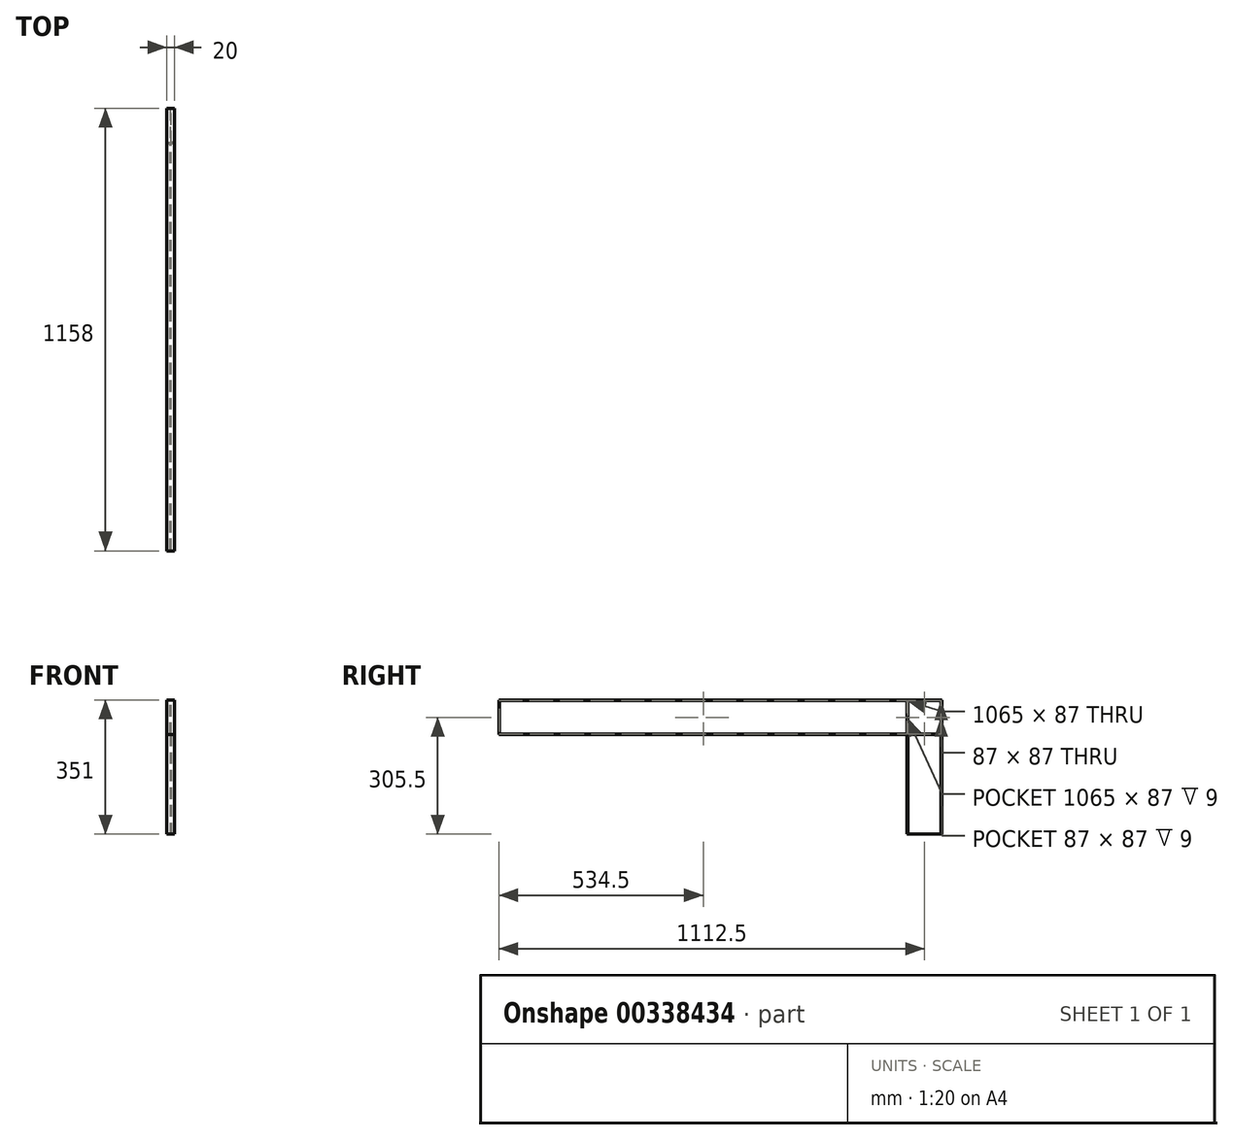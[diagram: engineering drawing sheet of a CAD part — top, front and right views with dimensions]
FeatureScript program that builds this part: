
annotation { "Feature Type Name" : "Feature", "Feature Type Description" : "" }
export const myFeature = defineFeature(function(context is Context, id is Id, definition is map)
    precondition{}
    {
        {
            var Q0;
            Q0=qCreatedBy(makeId("Top.planeOp"),FACE);
            var sketch = newSketch(context, id + "F0", { "sketchPlane" : qUnion([Q0])});
            skLineSegment(sketch, "E0.bottom", {"start": v(0, 0) * mm, "end": v(-20, 0) * mm});
            skLineSegment(sketch, "E0.top", {"start": v(0, 91) * mm, "end": v(-20, 91) * mm});
            skLineSegment(sketch, "E0.left", {"start": v(0, 0) * mm, "end": v(0, 2) * mm});
            skLineSegment(sketch, "E0.right", {"start": v(-20, 0) * mm, "end": v(-20, 2) * mm});
            skLineSegment(sketch, "E1", {"start": v(-20, 89) * mm, "end": v(-11, 89) * mm});
            skLineSegment(sketch, "E2", {"start": v(-20, 2) * mm, "end": v(-11, 2) * mm});
            skLineSegment(sketch, "E3", {"start": v(-11, 89) * mm, "end": v(-11, 2) * mm});
            skLineSegment(sketch, "E4", {"start": v(-9, 89) * mm, "end": v(-9, 2) * mm});
            skLineSegment(sketch, "E5.trimOffspring", {"start": v(-9, 89) * mm, "end": v(0, 89) * mm});
            skLineSegment(sketch, "E6.trimOffspring", {"start": v(-20, 89) * mm, "end": v(-20, 91) * mm});
            skLineSegment(sketch, "E7.trimOffspring", {"start": v(0, 89) * mm, "end": v(0, 91) * mm});
            skLineSegment(sketch, "E8.trimOffspring", {"start": v(-9, 2) * mm, "end": v(0, 2) * mm});
            skSolve(sketch);
        }
        {
            var Q0;
            Q0=makeQuery(id+"F0.imprint","IMPRINT",FACE,{"disambiguationData":[TD([[makeQuery(id+"F0.imprint","IMPRINT",EDGE,{"derivedFrom":sQuery(id+"F0.wireOp",EDGE,"E0.bottom")}),-1.0]])]});
            extrude(context, id + "F1", {"entities" : qUnion([Q0]), "depth" : 349 * mm});
        }
        {
            var Q0;
            Q0=makeQuery(id+"F1.opExtrude","CAP_FACE",FACE,{"disambiguationData":[OSD([sQuery(id+"F0.wireOp",EDGE,"E0.bottom"),sQuery(id+"F0.wireOp",EDGE,"E0.top"),sQuery(id+"F0.wireOp",EDGE,"E0.left"),sQuery(id+"F0.wireOp",EDGE,"E0.right"),sQuery(id+"F0.wireOp",EDGE,"E1"),sQuery(id+"F0.wireOp",EDGE,"E2"),sQuery(id+"F0.wireOp",EDGE,"E3"),sQuery(id+"F0.wireOp",EDGE,"E4"),sQuery(id+"F0.wireOp",EDGE,"E5.trimOffspring"),sQuery(id+"F0.wireOp",EDGE,"E6.trimOffspring"),sQuery(id+"F0.wireOp",EDGE,"E7.trimOffspring"),sQuery(id+"F0.wireOp",EDGE,"E8.trimOffspring")])],"isStart":false});
            var sketch = newSketch(context, id + "F2", { "sketchPlane" : qUnion([Q0])});
            skLineSegment(sketch, "E9.bottom", {"start": v(0, 0) * mm, "end": v(-20, 0) * mm});
            skLineSegment(sketch, "E9.top", {"start": v(0, 91) * mm, "end": v(-20, 91) * mm});
            skLineSegment(sketch, "E9.left", {"start": v(0, 0) * mm, "end": v(0, 91) * mm});
            skLineSegment(sketch, "E9.right", {"start": v(-20, 0) * mm, "end": v(-20, 91) * mm});
            skSolve(sketch);
        }
        {
            var Q0;
            {var subQ4=sQuery(id+"F2.wireOp",EDGE,"E9.bottom");Q0=makeQuery(id+"F2.imprint","IMPRINT",FACE,{"disambiguationData":[TD([[makeQuery(id+"F2.imprint","IMPRINT",EDGE,{"derivedFrom":subQ4}),-1.0]])]});}
            var Q1;
            {var subQ2=makeQuery(id+"F1.opExtrude","CAP_EDGE",EDGE,{"disambiguationData":[OSD([sQuery(id+"F0.wireOp",EDGE,"E1")])],"isStart":false});Q1=makeQuery(id+"F2.imprint","IMPRINT",FACE,{"disambiguationData":[TD([[makeQuery(id+"F2.imprint","IMPRINT",EDGE,{"derivedFrom":subQ2}),-1.0]])]});}
            var Q2;
            Q2=makeQuery(id+"F2.imprint","IMPRINT",FACE,{"disambiguationData":[TD([[makeQuery(id+"F2.imprint","IMPRINT",EDGE,{"derivedFrom":makeQuery(id+"F1.opExtrude","CAP_EDGE",EDGE,{"disambiguationData":[OSD([sQuery(id+"F0.wireOp",EDGE,"E4")])],"isStart":false})}),1.0]])]});
            extrude(context, id + "F3", {"entities" : qUnion([Q0, Q1, Q2]), "operationType" : NewBodyOperationType.ADD, "depth" : 2 * mm});
        }
        {
            var Q0;
            Q0=makeQuery(id+"F1.opExtrude","SWEPT_FACE",FACE,{"disambiguationData":[OSD([sQuery(id+"F0.wireOp",EDGE,"E3")])]});
            var sketch = newSketch(context, id + "F4", { "sketchPlane" : qUnion([Q0])});
            skLineSegment(sketch, "E10.bottom", {"start": v(-89, 349) * mm, "end": v(-2, 349) * mm});
            skLineSegment(sketch, "E10.top", {"start": v(-89, 262) * mm, "end": v(-2, 262) * mm});
            skLineSegment(sketch, "E10.left", {"start": v(-89, 349) * mm, "end": v(-89, 262) * mm});
            skLineSegment(sketch, "E10.right", {"start": v(-2, 349) * mm, "end": v(-2, 262) * mm});
            skLineSegment(sketch, "E11.top", {"start": v(-89, 260) * mm, "end": v(-2, 260) * mm});
            skLineSegment(sketch, "E11.left", {"start": v(-89, 262) * mm, "end": v(-89, 260) * mm});
            skLineSegment(sketch, "E11.right", {"start": v(-2, 262) * mm, "end": v(-2, 260) * mm});
            skSolve(sketch);
        }
        {
            var Q0;
            Q0=makeQuery(id+"F4.imprint","IMPRINT",FACE,{"disambiguationData":[TD([[makeQuery(id+"F4.imprint","IMPRINT",EDGE,{"derivedFrom":sQuery(id+"F4.wireOp",EDGE,"E10.top")}),-1.0]])]});
            var Q1;
            Q1=makeQuery(id+"F3.boolean.opBoolean","MERGE",FACE,{"derivedFrom":[makeQuery(id+"F1.opExtrude","SWEPT_FACE",FACE,{"disambiguationData":[OSD([sQuery(id+"F0.wireOp",EDGE,"E0.right")])]}),makeQuery(id+"F1.opExtrude","SWEPT_FACE",FACE,{"disambiguationData":[OSD([sQuery(id+"F0.wireOp",EDGE,"E6.trimOffspring")])]}),makeQuery(id+"F3.opExtrude","SWEPT_FACE",FACE,{"disambiguationData":[OSD([sQuery(id+"F2.wireOp",EDGE,"E9.right")])]})]});
            extrude(context, id + "F5", {"entities" : qUnion([Q0]), "operationType" : NewBodyOperationType.ADD, "endBound" : BoundingType.UP_TO_SURFACE, "endBoundEntityFace" : qUnion([Q1]), "depth" : 21.8 * mm});
        }
        {
            var Q0;
            Q0=makeQuery(id+"F4.imprint","IMPRINT",FACE,{"disambiguationData":[TD([[makeQuery(id+"F4.imprint","IMPRINT",EDGE,{"derivedFrom":sQuery(id+"F4.wireOp",EDGE,"E10.top")}),-1.0]])]});
            var Q1;
            Q1=makeQuery(id+"F3.boolean.opBoolean","MERGE",FACE,{"derivedFrom":[makeQuery(id+"F1.opExtrude","SWEPT_FACE",FACE,{"disambiguationData":[OSD([sQuery(id+"F0.wireOp",EDGE,"E0.left")])]}),makeQuery(id+"F1.opExtrude","SWEPT_FACE",FACE,{"disambiguationData":[OSD([sQuery(id+"F0.wireOp",EDGE,"E7.trimOffspring")])]}),makeQuery(id+"F3.opExtrude","SWEPT_FACE",FACE,{"disambiguationData":[OSD([sQuery(id+"F2.wireOp",EDGE,"E9.left")])]})]});
            extrude(context, id + "F6", {"entities" : qUnion([Q0]), "operationType" : NewBodyOperationType.ADD, "endBound" : BoundingType.UP_TO_SURFACE, "oppositeDirection" : true, "endBoundEntityFace" : qUnion([Q1]), "depth" : 7.3 * mm});
        }
        {
            var Q0;
            Q0=makeQuery(id+"F3.boolean.opBoolean","MERGE",FACE,{"derivedFrom":[makeQuery(id+"F1.opExtrude","SWEPT_FACE",FACE,{"disambiguationData":[OSD([sQuery(id+"F0.wireOp",EDGE,"E0.bottom")])]}),makeQuery(id+"F3.opExtrude","SWEPT_FACE",FACE,{"disambiguationData":[OSD([sQuery(id+"F2.wireOp",EDGE,"E9.bottom")])]})]});
            var sketch = newSketch(context, id + "F7", { "sketchPlane" : qUnion([Q0])});
            skLineSegment(sketch, "E12.bottom", {"start": v(-20, 351) * mm, "end": v(0, 351) * mm});
            skLineSegment(sketch, "E12.top", {"start": v(-20, 349) * mm, "end": v(-11, 349) * mm});
            skLineSegment(sketch, "E12.left", {"start": v(-20, 351) * mm, "end": v(-20, 349) * mm});
            skLineSegment(sketch, "E12.right", {"start": v(0, 351) * mm, "end": v(0, 349) * mm});
            skLineSegment(sketch, "E13.bottom", {"start": v(-20, 260) * mm, "end": v(0, 260) * mm});
            skLineSegment(sketch, "E13.top", {"start": v(-20, 262) * mm, "end": v(-11, 262) * mm});
            skLineSegment(sketch, "E13.left", {"start": v(-20, 260) * mm, "end": v(-20, 262) * mm});
            skLineSegment(sketch, "E13.right", {"start": v(0, 260) * mm, "end": v(0, 262) * mm});
            skLineSegment(sketch, "E14.left", {"start": v(-11, 262) * mm, "end": v(-11, 349) * mm});
            skLineSegment(sketch, "E14.right", {"start": v(-9, 262) * mm, "end": v(-9, 349) * mm});
            skLineSegment(sketch, "E15.trimOffspring", {"start": v(-9, 349) * mm, "end": v(0, 349) * mm});
            skLineSegment(sketch, "E16.trimOffspring", {"start": v(-9, 262) * mm, "end": v(0, 262) * mm});
            skSolve(sketch);
        }
        {
            var Q0;
            Q0=makeQuery(id+"F7.imprint","IMPRINT",FACE,{"disambiguationData":[TD([[makeQuery(id+"F7.imprint","IMPRINT",EDGE,{"derivedFrom":sQuery(id+"F7.wireOp",EDGE,"E12.bottom")}),1.0]])]});
            extrude(context, id + "F8", {"entities" : qUnion([Q0]), "operationType" : NewBodyOperationType.ADD, "depth" : 1067 * mm});
        }
        {
            var Q0;
            Q0=makeQuery(id+"F8.opExtrude","CAP_FACE",FACE,{"disambiguationData":[OSD([sQuery(id+"F7.wireOp",EDGE,"E12.bottom"),sQuery(id+"F7.wireOp",EDGE,"E12.top"),sQuery(id+"F7.wireOp",EDGE,"E12.left"),sQuery(id+"F7.wireOp",EDGE,"E12.right"),sQuery(id+"F7.wireOp",EDGE,"E13.bottom"),sQuery(id+"F7.wireOp",EDGE,"E13.top"),sQuery(id+"F7.wireOp",EDGE,"E13.left"),sQuery(id+"F7.wireOp",EDGE,"E13.right"),sQuery(id+"F7.wireOp",EDGE,"E14.left"),sQuery(id+"F7.wireOp",EDGE,"E14.right"),sQuery(id+"F7.wireOp",EDGE,"E15.trimOffspring"),sQuery(id+"F7.wireOp",EDGE,"E16.trimOffspring")])],"isStart":false});
            var sketch = newSketch(context, id + "F9", { "sketchPlane" : qUnion([Q0])});
            skLineSegment(sketch, "E17.bottom", {"start": v(-20, 351) * mm, "end": v(0, 351) * mm});
            skLineSegment(sketch, "E17.top", {"start": v(-20, 260) * mm, "end": v(0, 260) * mm});
            skLineSegment(sketch, "E17.left", {"start": v(-20, 351) * mm, "end": v(-20, 260) * mm});
            skLineSegment(sketch, "E17.right", {"start": v(0, 351) * mm, "end": v(0, 260) * mm});
            skSolve(sketch);
        }
        {
            var Q0;
            {var subQ1=makeQuery(id+"F8.opExtrude","CAP_EDGE",EDGE,{"disambiguationData":[OSD([sQuery(id+"F7.wireOp",EDGE,"E12.top")])],"isStart":false});Q0=makeQuery(id+"F9.imprint","IMPRINT",FACE,{"disambiguationData":[TD([[makeQuery(id+"F9.imprint","IMPRINT",EDGE,{"derivedFrom":subQ1}),-1.0]])]});}
            var Q1;
            Q1=makeQuery(id+"F9.imprint","IMPRINT",FACE,{"disambiguationData":[TD([[makeQuery(id+"F9.imprint","IMPRINT",EDGE,{"derivedFrom":makeQuery(id+"F8.opExtrude","CAP_EDGE",EDGE,{"disambiguationData":[OSD([sQuery(id+"F7.wireOp",EDGE,"E14.right")])],"isStart":false})}),-1.0]])]});
            extrude(context, id + "F10", {"entities" : qUnion([Q0, Q1]), "operationType" : NewBodyOperationType.ADD, "oppositeDirection" : true, "depth" : 2 * mm});
        }
    });
